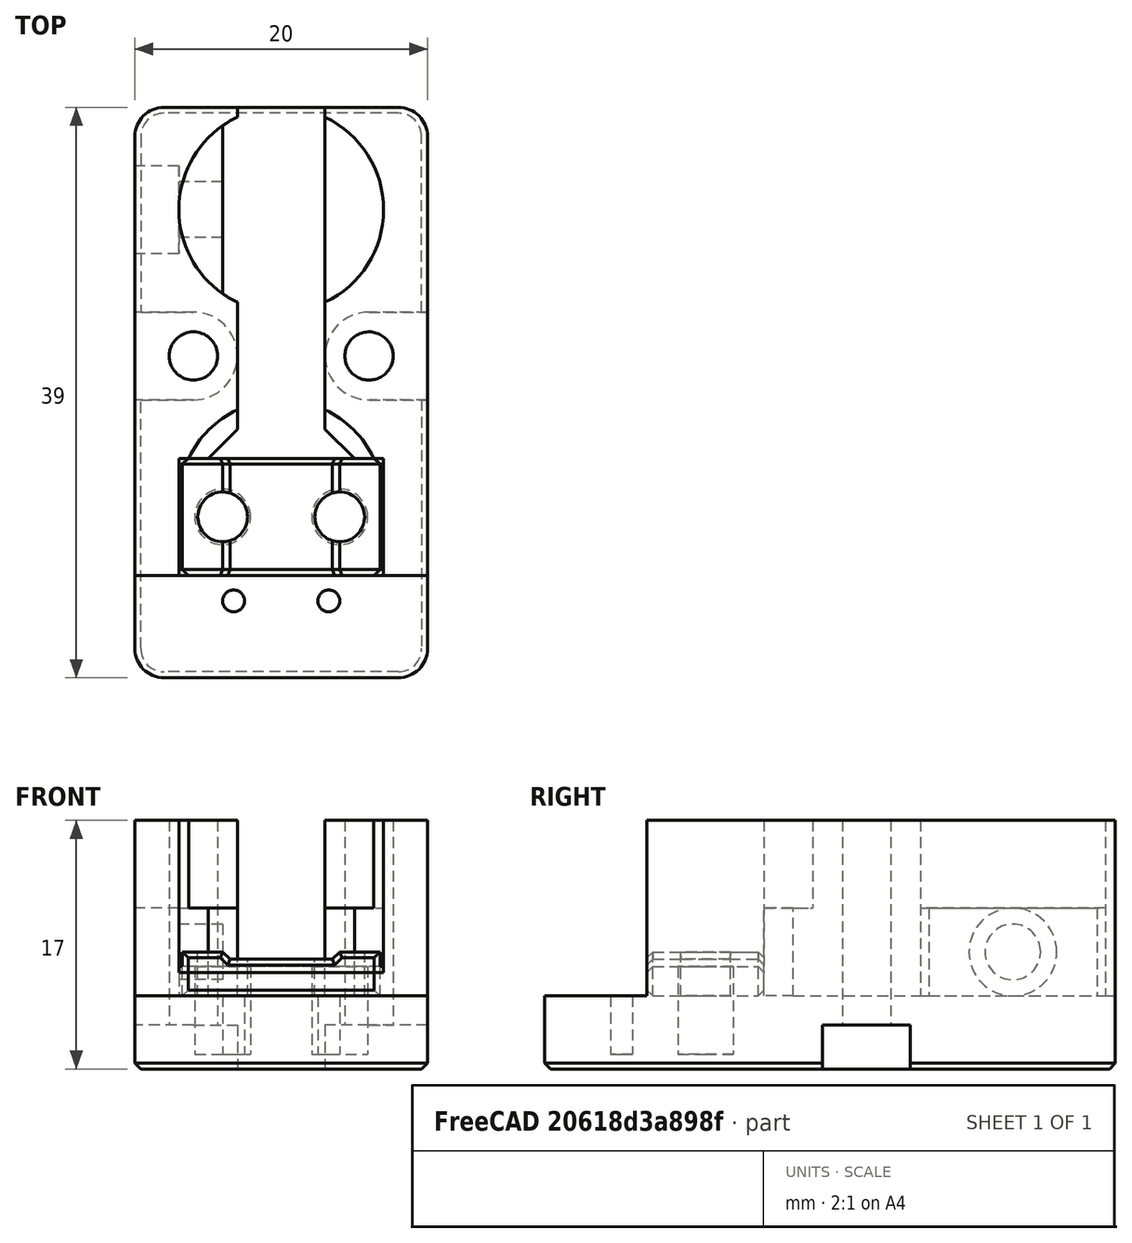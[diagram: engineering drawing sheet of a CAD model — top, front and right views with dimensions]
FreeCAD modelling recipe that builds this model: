
FCSTD DOCUMENT  (FreeCAD 0.19R24291 (Git))
Label: generic-chamber-sensor-mount
License: Other
LicenseURL: GPL3
objects: Part::Box×4, Part::Cut×4, Part::Cylinder×4, Part::MultiFuse×3, Part::Chamfer×3, Part::Feature×1, Part::Refine×1
note: 20 computed .brp shape members not serialized (recipe doc carries the construction recipe); baked Part::Feature solids carry a one-line shape summary decoded from their .brp

FEATURE [Part::Feature] Cut002008023012009006003002006002006002004004001  label="endstop-mount001"
  shape: bbox 20 x 39 x 17 mm, 57 faces (baked)
FEATURE [Part::Box] Box  label="Cube"
  AttacherType = Attacher::AttachEngine3D
  Height = 4
  Length = 14
  Placement = pos=(-7,7,8) rot=(0,0,1;0rad)
  Width = 8
FEATURE [Part::Box] Box001  label="Cube001"
  AttacherType = Attacher::AttachEngine3D
  Height = 13
  Length = 22
  Placement = pos=(-11,-1,-1) rot=(0,0,1;0rad)
  Width = 8
FEATURE [Part::Cut] Cut
  Base = -> Cut002008023012009006003002006002006002004004001
  Tool = -> Box001
FEATURE [Part::Cylinder] Cylinder
  Angle = 360
  AttacherType = Attacher::AttachEngine3D
  Height = 10
  Placement = pos=(-4,11,0) rot=(0,0,1;0rad)
  Radius = 1.9
FEATURE [Part::Cylinder] Cylinder001
  Angle = 360
  AttacherType = Attacher::AttachEngine3D
  Height = 10
  Placement = pos=(4,11,0) rot=(0,0,1;0rad)
  Radius = 1.9
FEATURE [Part::Cylinder] Cylinder002
  Angle = 360
  AttacherType = Attacher::AttachEngine3D
  Height = 10
  Placement = pos=(4,11,0) rot=(0,0,1;0rad)
  Radius = 1.7
FEATURE [Part::Cylinder] Cylinder003
  Angle = 360
  AttacherType = Attacher::AttachEngine3D
  Height = 10
  Placement = pos=(-4,11,0) rot=(0,0,1;0rad)
  Radius = 1.7
FEATURE [Part::Box] Box002  label="Cube002"
  AttacherType = Attacher::AttachEngine3D
  Height = 3
  Length = 13.5
  Placement = pos=(-6.75,7,5) rot=(0,0,1;0rad)
  Width = 8
FEATURE [Part::MultiFuse] Fusion
  Placement = pos=(0,0,6) rot=(0,0,1;0rad)
  Shapes = -> [Cylinder001,Cylinder]
FEATURE [Part::Box] Box003  label="Cube003"
  AttacherType = Attacher::AttachEngine3D
  Height = 1.5
  Length = 8
  Placement = pos=(-4,7,7.5) rot=(0,0,1;0rad)
  Width = 8
FEATURE [Part::Chamfer] Chamfer001
  Base = -> Box003
  Edges = 2 edges r=0.5: [Edge4,Edge8]
FEATURE [Part::Cut] Cut002008023012009006003002006002006002004004003
  Base = -> Box002
  Tool = -> Chamfer001
FEATURE [Part::MultiFuse] Fusion002
  Shapes = -> [Cylinder002,Cylinder003]
FEATURE [Part::Cut] Cut002008023012009006003002006002006002004004004
  Base = -> Cut002008023012009006003002006002006002004004003
  Tool = -> Fusion002
FEATURE [Part::Chamfer] Chamfer004
  Base = -> Cut002008023012009006003002006002006002004004004
  Edges = 16 edges r=0.4: [Edge1,Edge3,Edge5,Edge6,Edge7,Edge8,Edge9,Edge10,Edge11,Edge12,Edge16,Edge17,Edge18,Edge19,Edge20,Edge21]
FEATURE [Part::Chamfer] Chamfer
  Base = -> Box
  Edges = 2 edges r=0.4: [Edge9,Edge11]
  Placement = pos=(0,0,2) rot=(0,0,1;0rad)
FEATURE [Part::MultiFuse] Fusion003
  Shapes = -> [Chamfer,Cut]
FEATURE [Part::Cut] Cut002008023012009006003002006002006002004004005
  Base = -> Fusion003
  Tool = -> Fusion
FEATURE [Part::Refine] Cut002008023012009006003002006002006002004004005001
  Placement = pos=(-2.1e-15,0,17) rot=(0,1,0;3.14159rad)
  Source = -> Cut002008023012009006003002006002006002004004005
